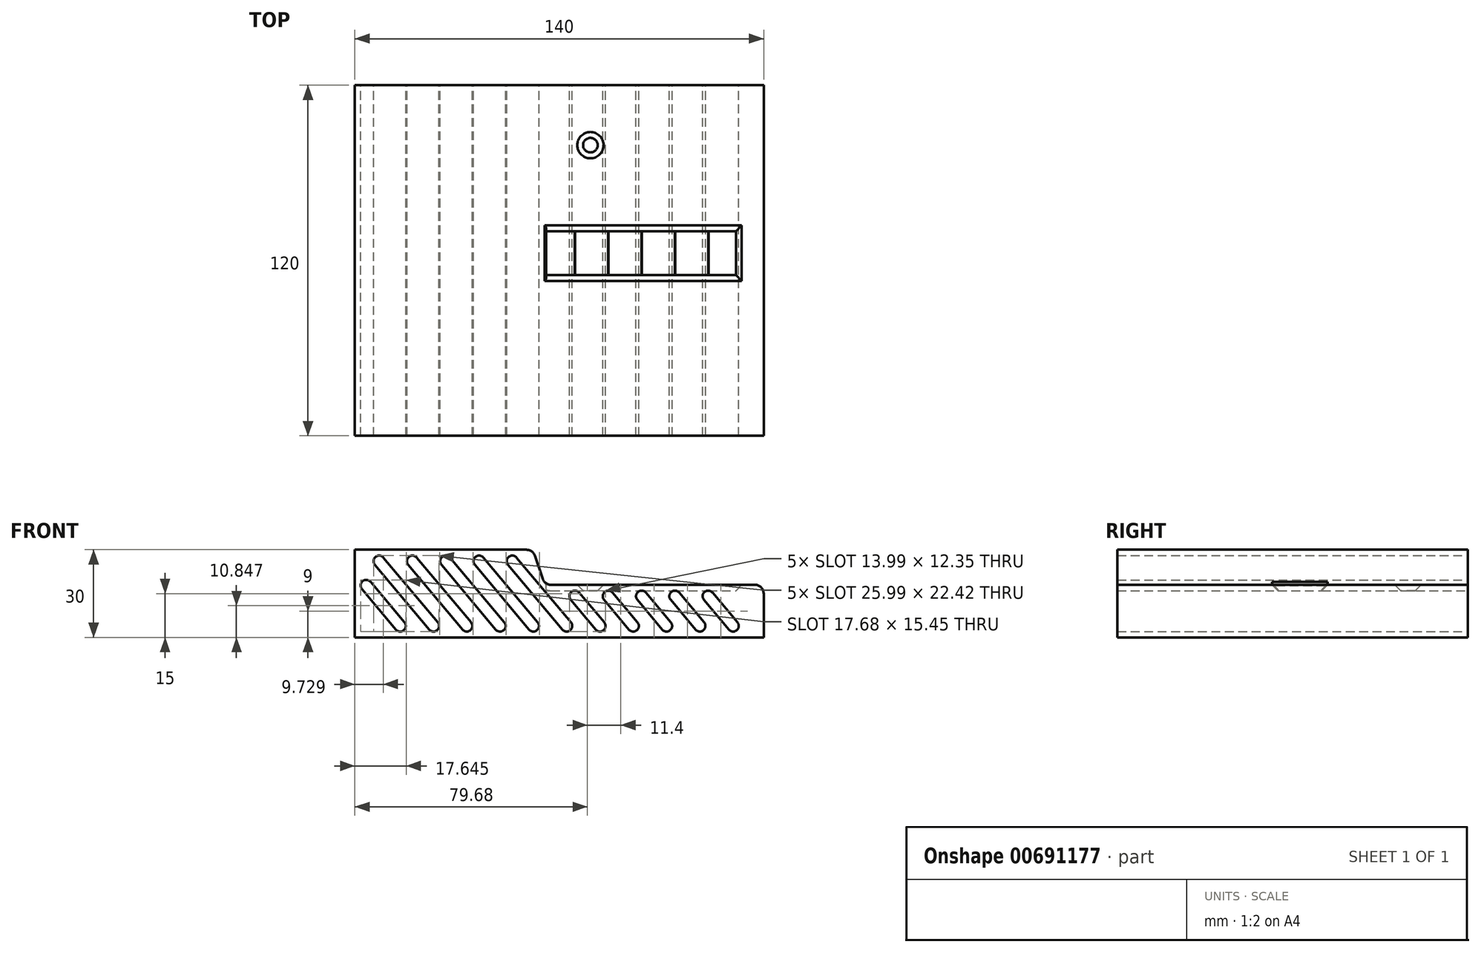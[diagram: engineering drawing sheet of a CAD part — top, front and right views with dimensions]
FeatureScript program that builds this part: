
annotation { "Feature Type Name" : "Feature", "Feature Type Description" : "" }
export const myFeature = defineFeature(function(context is Context, id is Id, definition is map)
    precondition{}
    {
        {
            var Q0;
            Q0=qCreatedBy(makeId("Front.planeOp"),FACE);
            var sketch = newSketch(context, id + "F0", { "sketchPlane" : qUnion([Q0])});
            skLineSegment(sketch, "E0", {"start": v(-70, 0) * mm, "end": v(70, 0) * mm});
            skLineSegment(sketch, "E1", {"start": v(70, 0) * mm, "end": v(70, 15) * mm});
            skLineSegment(sketch, "E2", {"start": v(67, 18) * mm, "end": v(-2.84, 18) * mm});
            skLineSegment(sketch, "E3", {"start": v(-5.68, 20.05) * mm, "end": v(-8.32, 27.95) * mm});
            skLineSegment(sketch, "E4", {"start": v(-11.16, 30) * mm, "end": v(-70, 30) * mm});
            skLineSegment(sketch, "E5", {"start": v(-70, 30) * mm, "end": v(-70, 0) * mm});
            skPoint(sketch, "E6.visualSharp", {"position": v(-9, 30) * mm});
            skArc(sketch, "E6.filletArc", {"start": v(-8.32, 27.95) * mm, "mid": v(-9.4, 29.43) * mm, "end": v(-11.16, 30) * mm});
            skPoint(sketch, "E7.visualSharp", {"position": v(-5, 18) * mm});
            skArc(sketch, "E7.filletArc", {"start": v(-5.68, 20.05) * mm, "mid": v(-4.6, 18.57) * mm, "end": v(-2.84, 18) * mm});
            skPoint(sketch, "E8.visualSharp", {"position": v(-70, 30) * mm});
            skPoint(sketch, "E9.visualSharp", {"position": v(70, 18) * mm});
            skArc(sketch, "E9.filletArc", {"start": v(70, 15) * mm, "mid": v(69.12, 17.12) * mm, "end": v(67, 18) * mm});
            skSolve(sketch);
        }
        {
            var Q0;
            Q0 = qSketchRegion(id + "F0", true);
            extrude(context, id + "F1", {"entities" : qUnion([Q0]), "endBound" : BoundingType.SYMMETRIC, "depth" : 120 * mm, "offsetDistance" : 25 * mm});
        }
        {
            var Q0;
            Q0=makeQuery(id+"FjGxbVABnygIQd1_1.opShell","OFFSET_FACE",FACE,{"disambiguationData":[OSD([sQuery(id+"F0.wireOp",EDGE,"E0")])]});
            var sketch = newSketch(context, id + "F2", { "sketchPlane" : qUnion([Q0])});
            skLineSegment(sketch, "E10.bottom", {"start": v(-68, 56) * mm, "end": v(-14.7, 56) * mm});
            skLineSegment(sketch, "E10.top", {"start": v(-68, -12.6) * mm, "end": v(-14.7, -12.6) * mm});
            skLineSegment(sketch, "E10.left", {"start": v(-68, 56) * mm, "end": v(-68, -12.6) * mm});
            skLineSegment(sketch, "E10.right", {"start": v(-14.7, 56) * mm, "end": v(-14.7, -12.6) * mm});
            skLineSegment(sketch, "E11.bottom", {"start": v(-68, -16.6) * mm, "end": v(-10.5, -16.6) * mm});
            skLineSegment(sketch, "E11.top", {"start": v(-68, -47.6) * mm, "end": v(-10.5, -47.6) * mm});
            skLineSegment(sketch, "E11.left", {"start": v(-68, -16.6) * mm, "end": v(-68, -47.6) * mm});
            skLineSegment(sketch, "E11.right", {"start": v(-10.5, -16.6) * mm, "end": v(-10.5, -47.6) * mm});
            skCircle(sketch, "E12", {"center": v(10.67, 39.5) * mm, "radius": 14 * mm});
            skLineSegment(sketch, "E13.bottom", {"start": v(45, 56) * mm, "end": v(66, 56) * mm});
            skLineSegment(sketch, "E13.top", {"start": v(45, 27) * mm, "end": v(66, 27) * mm});
            skLineSegment(sketch, "E13.left", {"start": v(45, 56) * mm, "end": v(45, 27) * mm});
            skLineSegment(sketch, "E13.right", {"start": v(66, 56) * mm, "end": v(66, 27) * mm});
            skLineSegment(sketch, "E14.bottom", {"start": v(68, 20.5) * mm, "end": v(-12, 20.5) * mm});
            skLineSegment(sketch, "E14.top", {"start": v(68, -15.5) * mm, "end": v(-12, -15.5) * mm});
            skLineSegment(sketch, "E14.left", {"start": v(68, 20.5) * mm, "end": v(68, -15.5) * mm});
            skLineSegment(sketch, "E14.right", {"start": v(-12, 20.5) * mm, "end": v(-12, -15.5) * mm});
            skLineSegment(sketch, "E15.bottom", {"start": v(9, -16.6) * mm, "end": v(53, -16.6) * mm});
            skLineSegment(sketch, "E15.top", {"start": v(9, -39.6) * mm, "end": v(53, -39.6) * mm});
            skLineSegment(sketch, "E15.left", {"start": v(9, -16.6) * mm, "end": v(9, -39.6) * mm});
            skLineSegment(sketch, "E15.right", {"start": v(53, -16.6) * mm, "end": v(53, -39.6) * mm});
            skLineSegment(sketch, "E16", {"start": v(-12, 2.5) * mm, "end": v(62.03, 2.5) * mm, "construction": true});
            skLineSegment(sketch, "E17.bottom", {"start": v(-4.5, -5) * mm, "end": v(60.5, -5) * mm});
            skLineSegment(sketch, "E17.top", {"start": v(-4.5, 10) * mm, "end": v(60.5, 10) * mm});
            skLineSegment(sketch, "E17.left", {"start": v(-4.5, -5) * mm, "end": v(-4.5, 10) * mm});
            skLineSegment(sketch, "E17.right", {"start": v(60.5, -5) * mm, "end": v(60.5, 10) * mm});
            skCircle(sketch, "E18", {"center": v(-22.4, 55) * mm, "radius": 1.5 * mm});
            skCircle(sketch, "E19", {"center": v(-50.3, 55) * mm, "radius": 1.5 * mm});
            skCircle(sketch, "E20", {"center": v(-17.2, 2.9) * mm, "radius": 1.5 * mm});
            skCircle(sketch, "E21", {"center": v(-65.5, 4.2) * mm, "radius": 1.5 * mm});
            skSolve(sketch);
        }
        {
            var Q0;
            Q0=makeQuery(id+"F1.opExtrude","SWEPT_FACE",FACE,{"disambiguationData":[OSD([sQuery(id+"F0.wireOp",EDGE,"E2")])]});
            var sketch = newSketch(context, id + "F3", { "sketchPlane" : qUnion([Q0])});
            skLineSegment(sketch, "E22.bottom", {"start": v(-4.5, 10) * mm, "end": v(60.5, 10) * mm});
            skLineSegment(sketch, "E22.top", {"start": v(-4.5, -5) * mm, "end": v(60.5, -5) * mm});
            skLineSegment(sketch, "E22.left", {"start": v(-4.5, 10) * mm, "end": v(-4.5, -5) * mm});
            skLineSegment(sketch, "E22.right", {"start": v(60.5, 10) * mm, "end": v(60.5, -5) * mm});
            skCircle(sketch, "E23", {"center": v(10.67, 39.5) * mm, "radius": 2.5 * mm});
            skSolve(sketch);
        }
        {
            var Q0;
            Q0=makeQuery(id+"F3.imprint","IMPRINT",FACE,{"disambiguationData":[TD([[makeQuery(id+"F3.imprint","IMPRINT",EDGE,{"derivedFrom":sQuery(id+"F3.wireOp",EDGE,"E23")}),1.0]])]});
            var Q1;
            Q1=makeQuery(id+"F3.imprint","IMPRINT",FACE,{"disambiguationData":[TD([[makeQuery(id+"F3.imprint","IMPRINT",EDGE,{"derivedFrom":sQuery(id+"F3.wireOp",EDGE,"E22.bottom")}),-1.0]])]});
            extrude(context, id + "F4", {"entities" : qUnion([Q0, Q1]), "operationType" : NewBodyOperationType.REMOVE, "endBound" : BoundingType.SYMMETRIC, "oppositeDirection" : true, "depth" : 4 * mm, "offsetDistance" : 25 * mm});
        }
        {
            var Q0;
            Q0=makeQuery(id+"F1.opExtrude","CAP_FACE",FACE,{"disambiguationData":[OSD([sQuery(id+"F0.wireOp",EDGE,"E0"),sQuery(id+"F0.wireOp",EDGE,"E1"),sQuery(id+"F0.wireOp",EDGE,"E2"),sQuery(id+"F0.wireOp",EDGE,"E3"),sQuery(id+"F0.wireOp",EDGE,"E4"),sQuery(id+"F0.wireOp",EDGE,"E5"),sQuery(id+"F0.wireOp",EDGE,"E6.filletArc"),sQuery(id+"F0.wireOp",EDGE,"E7.filletArc"),sQuery(id+"F0.wireOp",EDGE,"E8.filletArc"),sQuery(id+"F0.wireOp",EDGE,"E9.filletArc")])],"isStart":true});
            var sketch = newSketch(context, id + "F5", { "sketchPlane" : qUnion([Q0])});
            skLineSegment(sketch, "E24", {"start": v(-61.01, 5.15) * mm, "end": v(-52.48, 15.32) * mm});
            skLineSegment(sketch, "E25", {"start": v(-58.08, 2.68) * mm, "end": v(-49.55, 12.85) * mm});
            skArc(sketch, "E26", {"start": v(-49.55, 12.85) * mm, "mid": v(-49.78, 15.55) * mm, "end": v(-52.48, 15.32) * mm});
            skArc(sketch, "E27", {"start": v(-61.01, 5.15) * mm, "mid": v(-60.78, 2.45) * mm, "end": v(-58.08, 2.68) * mm});
            skLineSegment(sketch, "E28", {"start": v(-60.78, 2.45) * mm, "end": v(-52.25, 12.62) * mm, "construction": true});
            skPoint(sketch, "E29.orphan", {"position": v(-65.33, 0) * mm});
            skPoint(sketch, "E30.orphan", {"position": v(-60.33, 0) * mm});
            skPoint(sketch, "E31.orphan", {"position": v(-62.83, 0) * mm});
            skLineSegment(sketch, "E32.1.0.0", {"start": v(-46.68, 2.68) * mm, "end": v(-38.15, 12.85) * mm});
            skArc(sketch, "E32.1.0.1", {"start": v(-38.15, 12.85) * mm, "mid": v(-38.38, 15.55) * mm, "end": v(-41.08, 15.32) * mm});
            skLineSegment(sketch, "E32.1.0.2", {"start": v(-49.61, 5.15) * mm, "end": v(-41.08, 15.32) * mm});
            skArc(sketch, "E32.1.0.3", {"start": v(-49.61, 5.15) * mm, "mid": v(-49.38, 2.45) * mm, "end": v(-46.68, 2.68) * mm});
            skLineSegment(sketch, "E32.2.0.0", {"start": v(-35.28, 2.68) * mm, "end": v(-26.75, 12.85) * mm});
            skArc(sketch, "E32.2.0.1", {"start": v(-26.75, 12.85) * mm, "mid": v(-26.98, 15.55) * mm, "end": v(-29.68, 15.32) * mm});
            skLineSegment(sketch, "E32.2.0.2", {"start": v(-38.21, 5.15) * mm, "end": v(-29.68, 15.32) * mm});
            skArc(sketch, "E32.2.0.3", {"start": v(-38.21, 5.15) * mm, "mid": v(-37.98, 2.45) * mm, "end": v(-35.28, 2.68) * mm});
            skLineSegment(sketch, "E32.3.0.0", {"start": v(-23.88, 2.68) * mm, "end": v(-15.35, 12.85) * mm});
            skArc(sketch, "E32.3.0.1", {"start": v(-15.35, 12.85) * mm, "mid": v(-15.58, 15.55) * mm, "end": v(-18.28, 15.32) * mm});
            skLineSegment(sketch, "E32.3.0.2", {"start": v(-26.81, 5.15) * mm, "end": v(-18.28, 15.32) * mm});
            skArc(sketch, "E32.3.0.3", {"start": v(-26.81, 5.15) * mm, "mid": v(-26.58, 2.45) * mm, "end": v(-23.88, 2.68) * mm});
            skLineSegment(sketch, "E32.4.0.0", {"start": v(-12.48, 2.68) * mm, "end": v(-3.95, 12.85) * mm});
            skArc(sketch, "E32.4.0.1", {"start": v(-3.95, 12.85) * mm, "mid": v(-4.18, 15.55) * mm, "end": v(-6.88, 15.32) * mm});
            skLineSegment(sketch, "E32.4.0.2", {"start": v(-15.41, 5.15) * mm, "end": v(-6.88, 15.32) * mm});
            skArc(sketch, "E32.4.0.3", {"start": v(-15.41, 5.15) * mm, "mid": v(-15.18, 2.45) * mm, "end": v(-12.48, 2.68) * mm});
            skLineSegment(sketch, "E32.direction1", {"start": v(-58.08, 2.68) * mm, "end": v(-46.68, 2.68) * mm, "construction": true});
            skLineSegment(sketch, "E33", {"start": v(18.79, 5.15) * mm, "end": v(37.39, 27.32) * mm});
            skLineSegment(sketch, "E34", {"start": v(21.72, 2.68) * mm, "end": v(40.32, 24.85) * mm});
            skLineSegment(sketch, "E35", {"start": v(40.09, 27.55) * mm, "end": v(19.02, 2.45) * mm, "construction": true});
            skArc(sketch, "E36", {"start": v(18.79, 5.15) * mm, "mid": v(19.02, 2.45) * mm, "end": v(21.72, 2.68) * mm});
            skArc(sketch, "E37", {"start": v(40.32, 24.85) * mm, "mid": v(40.09, 27.55) * mm, "end": v(37.39, 27.32) * mm});
            skPoint(sketch, "E38.orphan", {"position": v(19.47, 0) * mm});
            skPoint(sketch, "E39.orphan", {"position": v(16.97, 0) * mm});
            skPoint(sketch, "E40.orphan", {"position": v(14.47, 0) * mm});
            skLineSegment(sketch, "E41.1.0.0", {"start": v(33.12, 2.68) * mm, "end": v(51.72, 24.85) * mm});
            skArc(sketch, "E41.1.0.1", {"start": v(51.72, 24.85) * mm, "mid": v(51.49, 27.55) * mm, "end": v(48.79, 27.32) * mm});
            skLineSegment(sketch, "E41.1.0.2", {"start": v(30.19, 5.15) * mm, "end": v(48.79, 27.32) * mm});
            skArc(sketch, "E41.1.0.3", {"start": v(30.19, 5.15) * mm, "mid": v(30.42, 2.45) * mm, "end": v(33.12, 2.68) * mm});
            skLineSegment(sketch, "E41.2.0.0", {"start": v(44.52, 2.68) * mm, "end": v(63.12, 24.85) * mm});
            skArc(sketch, "E41.2.0.1", {"start": v(63.12, 24.85) * mm, "mid": v(62.89, 27.55) * mm, "end": v(60.19, 27.32) * mm});
            skLineSegment(sketch, "E41.2.0.2", {"start": v(41.59, 5.15) * mm, "end": v(60.19, 27.32) * mm});
            skArc(sketch, "E41.2.0.3", {"start": v(41.59, 5.15) * mm, "mid": v(41.82, 2.45) * mm, "end": v(44.52, 2.68) * mm});
            skLineSegment(sketch, "E41.direction1", {"start": v(21.72, 2.68) * mm, "end": v(33.12, 2.68) * mm, "construction": true});
            skLineSegment(sketch, "E42", {"start": v(52.99, 5.15) * mm, "end": v(64.62, 19) * mm});
            skLineSegment(sketch, "E43", {"start": v(55.92, 2.68) * mm, "end": v(67.55, 16.55) * mm});
            skLineSegment(sketch, "E44", {"start": v(53.22, 2.45) * mm, "end": v(67.32, 19.25) * mm, "construction": true});
            skArc(sketch, "E45", {"start": v(52.99, 5.15) * mm, "mid": v(53.22, 2.45) * mm, "end": v(55.92, 2.68) * mm});
            skArc(sketch, "E46", {"start": v(67.55, 16.55) * mm, "mid": v(67.32, 19.25) * mm, "end": v(64.62, 19) * mm});
            skPoint(sketch, "E47.orphan", {"position": v(53.67, 0) * mm});
            skPoint(sketch, "E48.orphan", {"position": v(51.17, 0) * mm});
            skPoint(sketch, "E49.orphan", {"position": v(48.67, 0) * mm});
            skPoint(sketch, "E50.orphan", {"position": v(70, 25.42) * mm});
            skPoint(sketch, "E51.orphan", {"position": v(70, 22.44) * mm});
            skLineSegment(sketch, "E52.1.0.0", {"start": v(7.39, 5.15) * mm, "end": v(25.99, 27.32) * mm});
            skLineSegment(sketch, "E52.1.0.1", {"start": v(10.32, 2.68) * mm, "end": v(28.92, 24.85) * mm});
            skArc(sketch, "E52.1.0.2", {"start": v(28.92, 24.85) * mm, "mid": v(28.69, 27.55) * mm, "end": v(25.99, 27.32) * mm});
            skArc(sketch, "E52.1.0.3", {"start": v(7.39, 5.15) * mm, "mid": v(7.62, 2.45) * mm, "end": v(10.32, 2.68) * mm});
            skLineSegment(sketch, "E52.2.0.0", {"start": v(-4.01, 5.15) * mm, "end": v(14.59, 27.32) * mm});
            skLineSegment(sketch, "E52.2.0.1", {"start": v(-1.08, 2.68) * mm, "end": v(17.52, 24.85) * mm});
            skArc(sketch, "E52.2.0.2", {"start": v(17.52, 24.85) * mm, "mid": v(17.29, 27.55) * mm, "end": v(14.59, 27.32) * mm});
            skArc(sketch, "E52.2.0.3", {"start": v(-4.01, 5.15) * mm, "mid": v(-3.78, 2.45) * mm, "end": v(-1.08, 2.68) * mm});
            skLineSegment(sketch, "E52.direction1", {"start": v(18.79, 5.15) * mm, "end": v(7.39, 5.15) * mm, "construction": true});
            skSolve(sketch);
        }
        {
            var Q0;
            Q0 = qSketchRegion(id + "F5", true);
            extrude(context, id + "F6", {"entities" : qUnion([Q0]), "operationType" : NewBodyOperationType.REMOVE, "endBound" : BoundingType.THROUGH_ALL, "oppositeDirection" : true, "depth" : 25 * mm, "offsetDistance" : 25 * mm});
        }
        {
            var Q0;
            Q0=makeQuery(id+"F4.boolean.opBoolean","INTERSECT",EDGE,{"derivedFrom":[makeQuery(id+"F1.opExtrude","SWEPT_FACE",FACE,{"disambiguationData":[OSD([sQuery(id+"F0.wireOp",EDGE,"E2")])]}),makeQuery(id+"F4.opExtrude","SWEPT_FACE",FACE,{"disambiguationData":[OSD([sQuery(id+"F3.wireOp",EDGE,"E23")])]})]});
            var Q1;
            Q1=makeQuery(id+"F4.boolean.opBoolean","INTERSECT",EDGE,{"derivedFrom":[makeQuery(id+"F1.opExtrude","SWEPT_FACE",FACE,{"disambiguationData":[OSD([sQuery(id+"F0.wireOp",EDGE,"E2")])]}),makeQuery(id+"F4.opExtrude","SWEPT_FACE",FACE,{"disambiguationData":[OSD([sQuery(id+"F3.wireOp",EDGE,"E22.bottom")])]})]});
            var Q2;
            Q2=makeQuery(id+"F4.boolean.opBoolean","INTERSECT",EDGE,{"derivedFrom":[makeQuery(id+"F1.opExtrude","SWEPT_FACE",FACE,{"disambiguationData":[OSD([sQuery(id+"F0.wireOp",EDGE,"E7.filletArc")])]}),makeQuery(id+"F4.opExtrude","SWEPT_FACE",FACE,{"disambiguationData":[OSD([sQuery(id+"F3.wireOp",EDGE,"E22.left")])]})]});
            var Q3;
            Q3=makeQuery(id+"F4.boolean.opBoolean","INTERSECT",EDGE,{"derivedFrom":[makeQuery(id+"F1.opExtrude","SWEPT_FACE",FACE,{"disambiguationData":[OSD([sQuery(id+"F0.wireOp",EDGE,"E2")])]}),makeQuery(id+"F4.opExtrude","SWEPT_FACE",FACE,{"disambiguationData":[OSD([sQuery(id+"F3.wireOp",EDGE,"E22.top")])]})]});
            var Q4;
            Q4=makeQuery(id+"F4.boolean.opBoolean","INTERSECT",EDGE,{"derivedFrom":[makeQuery(id+"F1.opExtrude","SWEPT_FACE",FACE,{"disambiguationData":[OSD([sQuery(id+"F0.wireOp",EDGE,"E2")])]}),makeQuery(id+"F4.opExtrude","SWEPT_FACE",FACE,{"disambiguationData":[OSD([sQuery(id+"F3.wireOp",EDGE,"E22.right")])]})]});
            chamfer(context, id + "F7", {"entities" : qUnion([Q0, Q1, Q2, Q3, Q4]), "width" : 2 * mm, "tangentPropagation" : true});
        }
    });
